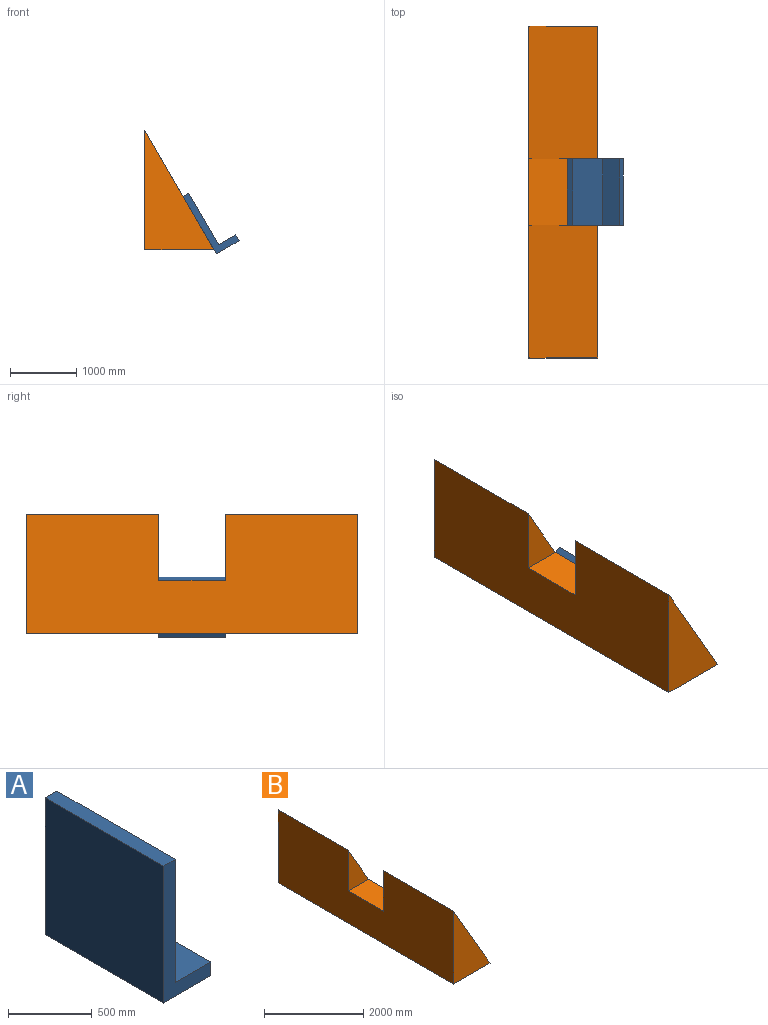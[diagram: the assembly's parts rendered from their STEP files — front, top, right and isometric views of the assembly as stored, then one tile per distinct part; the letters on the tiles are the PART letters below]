
ASSEMBLY  parts=2 mates=1
PART A: 8 faces, bbox 400x1000x1000 mm
  f0: plane 1000x1000mm, normal (-1,0,0), area 1000000mm2, adj f1,f5,f6,f7
  f1: plane 1000x400mm, normal (0,0,-1), area 400000mm2, adj f0,f2,f6,f7
  f2: plane 1000x100mm, normal (1,0,0), area 100000mm2, adj f1,f3,f6,f7
  f3: plane 1000x300mm, normal (0,0,1), area 300000mm2, adj f2,f4,f6,f7
  f4: plane 1000x900mm, normal (1,0,0), area 900000mm2, adj f3,f5,f6,f7
  f5: plane 1000x100mm, normal (0,0,1), area 100000mm2, adj f0,f4,f6,f7
  f6: plane 1000x400mm, normal (0,-1,0), area 130000mm2, adj f0,f1,f2,f3,f4,f5
  f7: plane 1000x400mm, normal (0,1,0), area 130000mm2, adj f0,f1,f2,f3,f4,f5
PART B: 74 faces, bbox 1039.2x5000x1800 mm
  f0: plane 5000x1800mm, normal (0.87,0,0.5), area 9157284mm2, adj f1,f2,f3,f4,f5,f6,f7,f12
  f1: plane 5000x1800mm, normal (-1,0,0), area 8000000mm2, adj f0,f2,f3,f4,f5,f6,f7
  f2: plane 5000x1039.23mm, normal (0,0,-1), area 5196152.4mm2, adj f0,f1,f3,f4
  f3: plane 1800x1039.23mm, normal (0,-1,0), area 935307.4mm2, adj f0,f1,f2
  f4: plane 1800x1039.23mm, normal (0,1,0), area 935307.4mm2, adj f0,f1,f2
  f5: plane 1000x577.35mm, normal (0,-1,0), area 288675.1mm2, adj f0,f1,f7
  f6: plane 1000x577.35mm, normal (0,1,0), area 288675.1mm2, adj f0,f1,f7
  f7: plane 1000x577.35mm, normal (0,0,1), area 577350.3mm2, adj f0,f1,f5,f6
  f8: plane 100.78x87.05mm, normal (0.18,-0.94,-0.3), area 4673.6mm2, adj f9,f20,f21,f22
  f9: plane 91.33x43.3mm, normal (-0.5,0,0.87), area 4566.5mm2, adj f8,f10,f21,f22
  f10: plane 100.78x87.05mm, normal (0.18,0.94,-0.31), area 4679mm2, adj f9,f11,f21,f22
  f11: extruded ~63.66x60.27mm, area 2126.3mm2, adj f10,f20,f21,f22
  f12: plane 102.76x88.19mm, normal (0.18,-0.93,-0.32), area 4821.3mm2, adj f0,f13,f19,f21
  f13: plane 43.3x33.99mm, normal (0.5,0,-0.87), area 1699.3mm2, adj f0,f12,f14,f21
  f14: plane 270.53x185.06mm, normal (-0.18,0.93,0.32), area 15224mm2, adj f0,f13,f15,f21
  f15: plane 43.3x27.62mm, normal (-0.5,0,0.87), area 1381.1mm2, adj f0,f14,f16,f21
  f16: plane 270.53x185.06mm, normal (-0.18,-0.93,0.32), area 15234.2mm2, adj f0,f15,f17,f21
  f17: plane 43.3x33.25mm, normal (0.5,0,-0.87), area 1662.2mm2, adj f0,f16,f18,f21
  f18: plane 102.76x88.19mm, normal (0.18,0.93,-0.31), area 4813.4mm2, adj f0,f17,f19,f21
  f19: plane 113.14x43.3mm, normal (0.5,0,-0.87), area 5657.2mm2, adj f0,f12,f18,f21
  f20: extruded ~63.66x60.27mm, area 2139.6mm2, adj f8,f11,f21,f22
  f21: plane 250.26x245.53mm, normal (0.87,0,0.5), area 20510.4mm2, adj f8,f9,f10,f11,f12,f13,f14,f15
  f22: plane 111.04x91.33mm, normal (0.87,0,0.5), area 5584.9mm2, adj f8,f9,f10,f11,f20
  f23: plane 43.3x32.07mm, normal (0.5,0,-0.87), area 1603.5mm2, adj f0,f24,f26,f27
  f24: plane 285.24x193.55mm, normal (0,1,0), area 15025.1mm2, adj f0,f23,f25,f27
  f25: plane 43.3x32.07mm, normal (-0.5,0,0.87), area 1603.5mm2, adj f0,f24,f26,f27
  f26: plane 285.24x193.55mm, normal (0,-1,0), area 15025.1mm2, adj f0,f23,f25,f27
  f27: plane 260.24x150.25mm, normal (0.87,0,0.5), area 9637.4mm2, adj f23,f24,f25,f26
  f28: plane 43.3x32.07mm, normal (0.5,0,-0.87), area 1603.5mm2, adj f0,f29,f31,f32
  f29: plane 208.29x149.12mm, normal (0,1,0), area 10582.2mm2, adj f0,f28,f30,f32
  f30: plane 43.3x32.07mm, normal (-0.5,0,0.87), area 1603.5mm2, adj f0,f29,f31,f32
  f31: plane 208.29x149.12mm, normal (0,-1,0), area 10582.2mm2, adj f0,f28,f30,f32
  f32: plane 183.29x105.82mm, normal (0.87,0,0.5), area 6787.6mm2, adj f28,f29,f30,f31
  f33: extruded ~51.37x38.97mm, area 874.5mm2, adj f0,f34,f40,f41
  f34: extruded ~51.37x38.97mm, area 873.6mm2, adj f0,f33,f35,f41
  f35: extruded ~45.96x29.6mm, area 748.2mm2, adj f0,f34,f36,f41
  f36: extruded ~45.96x29.6mm, area 735.5mm2, adj f0,f35,f37,f41
  f37: extruded ~51.37x38.97mm, area 877.9mm2, adj f0,f36,f38,f41
  f38: extruded ~51.32x38.89mm, area 873.9mm2, adj f0,f37,f39,f41
  f39: extruded ~45.91x29.52mm, area 733.3mm2, adj f0,f38,f40,f41
  f40: extruded ~45.87x29.44mm, area 743.8mm2, adj f0,f33,f39,f41
  f41: plane 37.88x36.98mm, normal (0.87,0,0.5), area 1319.1mm2, adj f33,f34,f35,f36,f37,f38,f39,f40
  f42: plane 153.56x43.3mm, normal (0.5,0,-0.87), area 7677.9mm2, adj f0,f43,f51,f52
  f43: plane 55.75x46.57mm, normal (0,1,0), area 1245.1mm2, adj f0,f42,f44,f52
  f44: plane 116.85x43.3mm, normal (-0.5,0,0.87), area 5842.6mm2, adj f0,f43,f45,f52
  f45: plane 165.16x124.22mm, normal (0.29,0.82,-0.5), area 9896.4mm2, adj f0,f44,f46,f52
  f46: plane 55.75x46.57mm, normal (0,1,0), area 1245.1mm2, adj f0,f45,f47,f52
  f47: plane 143.48x43.3mm, normal (-0.5,0,0.87), area 7174.2mm2, adj f0,f46,f48,f52
  f48: plane 55.75x46.57mm, normal (0,-1,0), area 1245.1mm2, adj f0,f47,f49,f52
  f49: plane 108.32x43.3mm, normal (0.5,0,-0.87), area 5416.2mm2, adj f0,f48,f50,f52
  f50: plane 167.83x125.77mm, normal (-0.29,-0.82,0.5), area 10067.2mm2, adj f0,f49,f51,f52
  f51: plane 54.21x43.89mm, normal (0,-1,0), area 1090.7mm2, adj f0,f42,f50,f52
  f52: plane 183.29x153.56mm, normal (0.87,0,0.5), area 13034.1mm2, adj f42,f43,f44,f45,f46,f47,f48,f49
  f53: extruded ~51.6x40.63mm, area 2263mm2, adj f54,f71,f72,f73
  f54: extruded ~51.37x38.97mm, area 2166.9mm2, adj f53,f55,f72,f73
  f55: extruded ~66.5x65.19mm, area 2466.1mm2, adj f54,f56,f72,f73
  f56: plane 110.67x43.3mm, normal (-0.5,0,0.87), area 5533.6mm2, adj f55,f71,f72,f73
  f57: extruded ~74.06x57.61mm, area 4087.2mm2, adj f0,f58,f70,f72
  f58: extruded ~44.91x36.58mm, area 1839.4mm2, adj f0,f57,f59,f72
  f59: extruded ~48.55x34.1mm, area 1693mm2, adj f0,f58,f60,f72
  f60: plane 57.61x49.78mm, normal (0,1,0), area 1430.5mm2, adj f0,f59,f61,f72
  f61: extruded ~67.54x50.44mm, area 3475.6mm2, adj f0,f60,f62,f72
  f62: extruded ~52.96x50.3mm, area 2776.1mm2, adj f0,f61,f63,f72
  f63: extruded ~73.99x71.59mm, area 3047.2mm2, adj f0,f62,f64,f72
  f64: plane 145.77x43.3mm, normal (0.5,0,-0.87), area 7288.6mm2, adj f0,f63,f65,f72
  f65: plane 53.44x42.55mm, normal (0,1,0), area 1013.4mm2, adj f0,f64,f66,f72
  f66: extruded ~84.8x77.83mm, area 3726mm2, adj f0,f65,f67,f72
  f67: extruded ~62.91x56.39mm, area 3517.7mm2, adj f0,f66,f68,f72
  f68: extruded ~67.73x58.36mm, area 3836.5mm2, adj f0,f67,f69,f72
  f69: extruded ~95.45x83.98mm, area 4347.9mm2, adj f0,f68,f70,f72
  f70: extruded ~93.71x82.97mm, area 4299.2mm2, adj f0,f57,f69,f72
  f71: extruded ~66.27x64.79mm, area 2509.6mm2, adj f53,f56,f72,f73
  f72: plane 190.03x179.02mm, normal (0.87,0,0.5), area 17867.9mm2, adj f53,f54,f55,f56,f57,f58,f59,f60
  f73: plane 110.67x54.16mm, normal (0.87,0,0.5), area 5579mm2, adj f53,f54,f55,f56,f71
PLACE A rot(axis=(0,-1,0),30deg) t=(-836.89,-261.3,-150.19)mm
PLACE B t=(-875.01,-261.3,-84.17)mm fixed
MATE revolute A.f6 <-> B.f6  axis (0,-1,0) through (-1336.89,-761.3,715.83)mm
